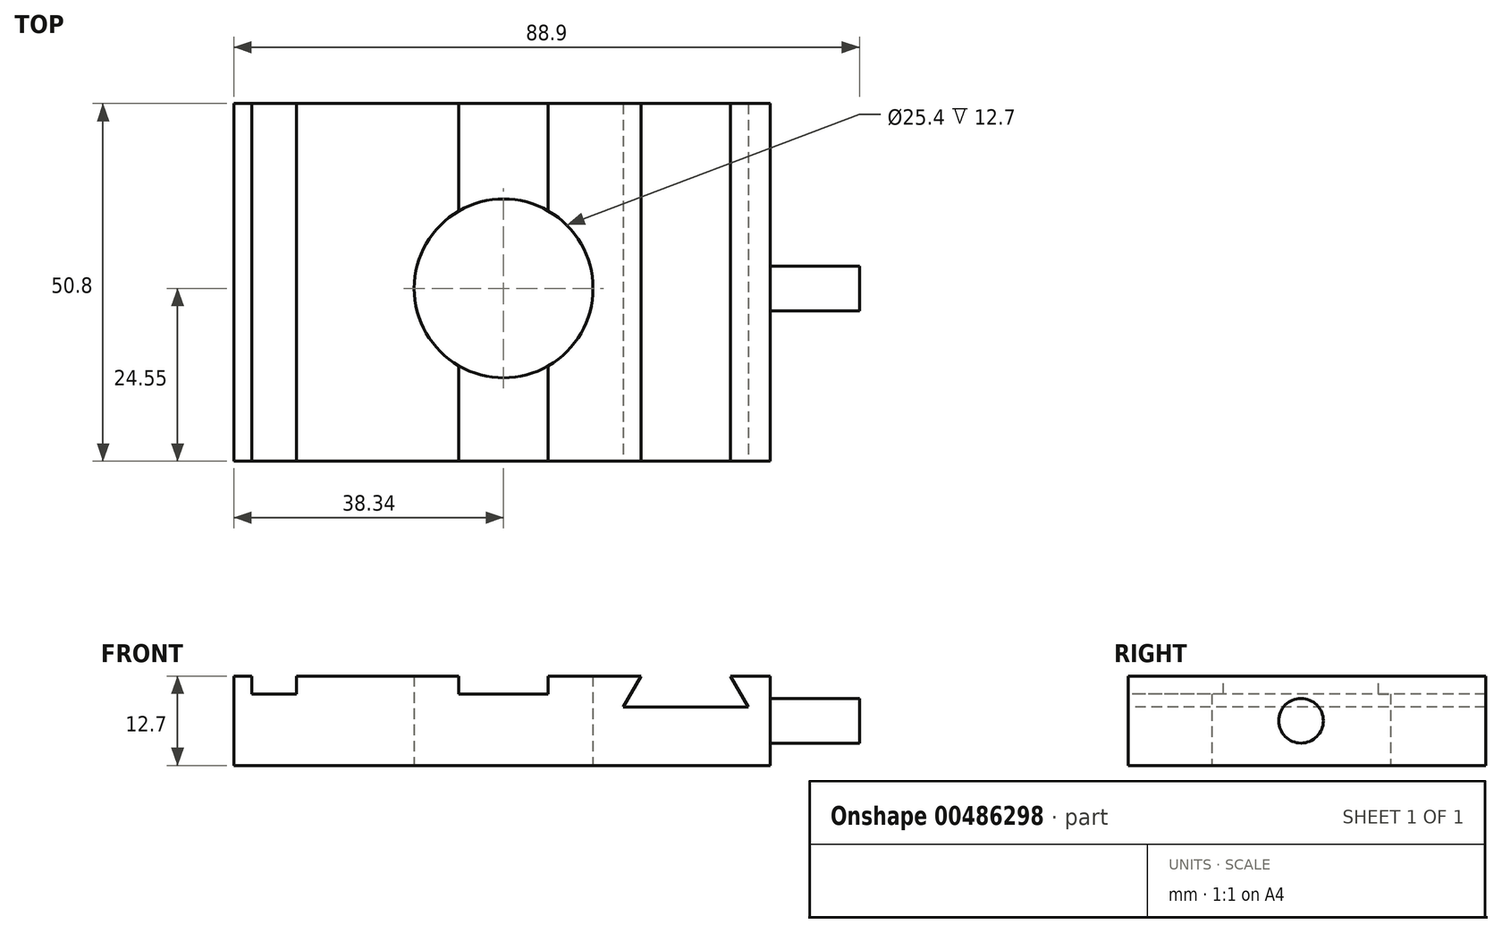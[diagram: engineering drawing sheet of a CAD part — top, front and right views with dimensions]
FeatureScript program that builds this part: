
annotation { "Feature Type Name" : "Feature", "Feature Type Description" : "" }
export const myFeature = defineFeature(function(context is Context, id is Id, definition is map)
    precondition{}
    {
        {
            var Q0;
            Q0=qCreatedBy(makeId("Top.planeOp"),FACE);
            var sketch = newSketch(context, id + "F0", { "sketchPlane" : qUnion([Q0])});
            skLineSegment(sketch, "E0.bottom", {"start": v(-38.34, 26.25) * mm, "end": v(37.86, 26.25) * mm});
            skLineSegment(sketch, "E0.top", {"start": v(-38.34, -24.55) * mm, "end": v(37.86, -24.55) * mm});
            skLineSegment(sketch, "E0.left", {"start": v(-38.34, 26.25) * mm, "end": v(-38.34, -24.55) * mm});
            skLineSegment(sketch, "E0.right", {"start": v(37.86, 26.25) * mm, "end": v(37.86, -24.55) * mm});
            skCircle(sketch, "E1", {"center": v(0, 0) * mm, "radius": 12.7 * mm});
            skSolve(sketch);
        }
        {
            var Q0;
            Q0=makeQuery(id+"F0.imprint","IMPRINT",FACE,{"disambiguationData":[TD([[makeQuery(id+"F0.imprint","IMPRINT",EDGE,{"derivedFrom":sQuery(id+"F0.wireOp",EDGE,"E0.bottom")}),-1.0]])]});
            extrude(context, id + "F1", {"entities" : qUnion([Q0]), "depth" : 12.7 * mm, "offsetDistance" : 25.4 * mm});
        }
        {
            var Q0;
            Q0=makeQuery(id+"F1.opExtrude","CAP_FACE",FACE,{"disambiguationData":[OSD([sQuery(id+"F0.wireOp",EDGE,"E0.bottom"),sQuery(id+"F0.wireOp",EDGE,"E0.top"),sQuery(id+"F0.wireOp",EDGE,"E0.left"),sQuery(id+"F0.wireOp",EDGE,"E0.right"),sQuery(id+"F0.wireOp",EDGE,"E1")])],"isStart":false});
            var sketch = newSketch(context, id + "F2", { "sketchPlane" : qUnion([Q0])});
            skLineSegment(sketch, "E2.bottom", {"start": v(-6.35, 26.25) * mm, "end": v(6.35, 26.25) * mm});
            skLineSegment(sketch, "E2.top", {"start": v(-6.35, -24.55) * mm, "end": v(6.35, -24.55) * mm});
            skLineSegment(sketch, "E2.left", {"start": v(-6.35, 26.25) * mm, "end": v(-6.35, -24.55) * mm});
            skLineSegment(sketch, "E2.right", {"start": v(6.35, 26.25) * mm, "end": v(6.35, -24.55) * mm});
            skPoint(sketch, "E3", {"position": v(6.35, 0) * mm});
            skLineSegment(sketch, "E4", {"start": v(0, 26.25) * mm, "end": v(0, -24.55) * mm, "construction": true});
            skLineSegment(sketch, "E5.bottom", {"start": v(-35.8, 26.25) * mm, "end": v(-29.45, 26.25) * mm});
            skLineSegment(sketch, "E5.top", {"start": v(-35.8, -24.55) * mm, "end": v(-29.45, -24.55) * mm});
            skLineSegment(sketch, "E5.left", {"start": v(-35.8, 26.25) * mm, "end": v(-35.8, -24.55) * mm});
            skLineSegment(sketch, "E5.right", {"start": v(-29.45, 26.25) * mm, "end": v(-29.45, -24.55) * mm});
            skSolve(sketch);
        }
        {
            var Q0;
            {var subQ0=sQuery(id+"F2.wireOp",EDGE,"E2.bottom");Q0=makeQuery(id+"F2.imprint","IMPRINT",FACE,{"disambiguationData":[TD([[makeQuery(id+"F2.imprint","IMPRINT",EDGE,{"derivedFrom":subQ0}),-1.0]])]});}
            var Q1;
            {var subQ0=sQuery(id+"F2.wireOp",EDGE,"E2.top");Q1=makeQuery(id+"F2.imprint","IMPRINT",FACE,{"disambiguationData":[TD([[makeQuery(id+"F2.imprint","IMPRINT",EDGE,{"derivedFrom":subQ0}),1.0]])]});}
            var Q2;
            Q2=makeQuery(id+"F2.imprint","IMPRINT",FACE,{"disambiguationData":[TD([[makeQuery(id+"F2.imprint","IMPRINT",EDGE,{"derivedFrom":sQuery(id+"F2.wireOp",EDGE,"E5.bottom")}),-1.0]])]});
            var Q3;
            Q3 = qSketchRegion(id + "F4", true);
            extrude(context, id + "F3", {"entities" : qUnion([Q0, Q1, Q2, Q3]), "operationType" : NewBodyOperationType.REMOVE, "oppositeDirection" : true, "depth" : 2.54 * mm, "offsetDistance" : 25.4 * mm});
        }
        {
            var Q0;
            Q0=makeQuery(id+"F1.opExtrude","SWEPT_FACE",FACE,{"disambiguationData":[OSD([sQuery(id+"F0.wireOp",EDGE,"E0.top")])]});
            var sketch = newSketch(context, id + "F4", { "sketchPlane" : qUnion([Q0])});
            skLineSegment(sketch, "E6", {"start": v(19.55, 12.7) * mm, "end": v(17, 8.3) * mm});
            skLineSegment(sketch, "E7", {"start": v(19.55, 12.7) * mm, "end": v(32.25, 12.7) * mm});
            skLineSegment(sketch, "E8", {"start": v(32.25, 12.7) * mm, "end": v(34.79, 8.3) * mm});
            skLineSegment(sketch, "E9", {"start": v(34.79, 8.3) * mm, "end": v(17, 8.3) * mm});
            skSolve(sketch);
        }
        {
            var Q0;
            Q0=makeQuery(id+"F4.imprint","IMPRINT",FACE,{"disambiguationData":[TD([[makeQuery(id+"F4.imprint","IMPRINT",EDGE,{"derivedFrom":sQuery(id+"F4.wireOp",EDGE,"E6")}),1.0]])]});
            var Q1;
            Q1=sQuery(id+"F4.wireOp",EDGE,"E6");
            var Q2;
            Q2=sQuery(id+"F4.wireOp",EDGE,"E7");
            var Q3;
            Q3=sQuery(id+"F4.wireOp",EDGE,"E8");
            var Q4;
            Q4=sQuery(id+"F4.wireOp",EDGE,"E9");
            extrude(context, id + "F5", {"entities" : qUnion([Q0]), "operationType" : NewBodyOperationType.REMOVE, "surfaceEntities" : qUnion([Q1, Q2, Q3, Q4]), "oppositeDirection" : true, "depth" : 58 * mm, "offsetDistance" : 25.4 * mm});
        }
        {
            var Q0;
            Q0=makeQuery(id+"F1.opExtrude","SWEPT_FACE",FACE,{"disambiguationData":[OSD([sQuery(id+"F0.wireOp",EDGE,"E0.right")])]});
            var sketch = newSketch(context, id + "F6", { "sketchPlane" : qUnion([Q0])});
            skCircle(sketch, "E10", {"center": v(0, 6.35) * mm, "radius": 3.18 * mm});
            skPoint(sketch, "E10.centerSnap0", {"position": v(-24.55, 6.35) * mm});
            skSolve(sketch);
        }
        {
            var Q0;
            Q0=makeQuery(id+"F6.imprint","IMPRINT",FACE,{"disambiguationData":[TD([[makeQuery(id+"F6.imprint","IMPRINT",EDGE,{"derivedFrom":sQuery(id+"F6.wireOp",EDGE,"E10")}),1.0]])]});
            extrude(context, id + "F7", {"entities" : qUnion([Q0]), "operationType" : NewBodyOperationType.ADD, "depth" : 12.7 * mm, "offsetDistance" : 25.4 * mm});
        }
    });
